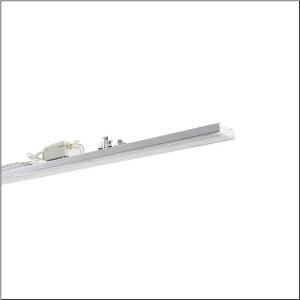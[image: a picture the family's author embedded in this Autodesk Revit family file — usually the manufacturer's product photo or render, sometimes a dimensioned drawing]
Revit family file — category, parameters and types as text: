
# Revit family: licross_r__21_recessed_mo_52tl127n455g_0cc2
name_source: partatom
category: Lighting Fixtures
units: mm (PartAtom-declared; Revit-internal decimal feet)

## family parameters
Cut with Voids When Loaded = No
Host = Face
Light Source = No
Part Type = Normal
Room Calculation Point = No
Round Connector Dimension = Use Diameter
Shared = No

## types (1)
- Licross® 21 Recessed MO (1 x LED, 5600 lm, 29.8 W, 4000K)
    Apparent Load = 30 VA
    CIE Flux Codes = 72 92 99 100 100
    Color Rendering = 80
    Color Temperature = 4000K
    Default Elevation = 1800 mm
    Description = Licross® 21 Recessed MO, luminaire insert, of sheet steel, galvanised, coil coated, white, length: 1.500mm, width: 66mm, height: 67mm, LED rated luminous flux: 5.600lm, light colour: 840, SDCM (Standard Deviation of Colour Matching)MacAdam ≤ 3 SDCM (initial), control gear: ON/OFF, with plug, 3-pole, with phase selection, mains connection: 220..240V, AC, 50/60Hz, rated input power: 30W, internal wiring halogen-free, primary optical cover: cover, of PMMA, light emission: direct distribution, primary light characteristic: symmetric, protection rating (complete): IP40, insulation class (complete): insulation class I (protective earthing), certification: CE, ENEC, VDE, UKCA, protection symbol: D if used in an environment without relevant dust loads with corresponding accessories, impact resistance: IK06, permissible ambient temperature for indoor applications: -35..+50°C, corresponds to IFS (International Featured Standards) requirements for safety and quality in the food industry, reducing of maximum allowable ambient temperature of 5°C with ceiling mounting, LABS conformity tested according to VDMA 24364:2018-05, packaging unit: 1 piece
    Height = 58 mm
    Lamp = 1 x LED
    Lamp Light Flux = 5600 lm
    Lamp Power = 29.8 W
    Lamp count = 1
    Length = 1500 mm
    Luminous efficacy = 188 lm/W
    Manufacturer = Siteco
    ModVariant = No
    Model = 52TL127N455G
    Mounting Place = Ceiling
    Mounting Type = Pendant
    Number of Poles = 1
    OnlyDefault = Yes
    Power Factor = 1
    Product Name = Licross® 21 Recessed MO
    Product group = luminaire insert | ceiling pendant
    ProductGroupID = 901
    Protection Class = Protection class I
    Protection Degree = IP 40
    RLX_Detail_Level = 1
    RLX_Emergency_Light_Flux = 0 lm
    RLX_Emergency_Type = 0
    RLX_Emergency_Type_DB = No
    RlxData = <blob elided: 21033 chars, md5=5283f626>
    Socket = socket
    Standby Power = 0 W
    System Light Flux = 5600 lm
    System Power = 30 W
    Type Comments = Product without accessories
    Type Image = l_1296930.jpg
    URL = http://relux.com
    VarID = ---
    Voltage = 0 V
    Weight = 0.00 kg
    Width = 66 mm

## geometry (parser evidence)
native form markers: Blend x4, Sweep x9
no freeform markers — native parametric forms only
